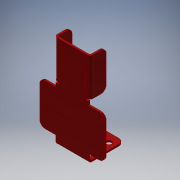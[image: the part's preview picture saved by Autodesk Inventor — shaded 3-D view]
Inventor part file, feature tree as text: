
AUTODESK INVENTOR PART (.ipt)
format: ipt  version: 2018 (Build 220112000, 112)  size: 207,872 bytes
history: native  units: mm
features: other x28, sketch x7, reference x4, hole x1
ambient origin geometry x8: Origin, YZ Plane, XZ Plane, XY Plane, X Axis, Y Axis, Z Axis, Center Point
bodies: Solido1 (feature_tree)
feature tree (40):
  other  "Supporto pistone pinza"
  other  "Faccia1"
  other  "Flangia1"
  hole  "Foro1"  [1 undecoded]
  other  "Flangia3"
  other  "Flangia4"
  other  "Flangia5"
  other  "Flangia6"
  other  "Arrotondamento angolo1"
  sketch  "Schizzo1"
  other  "Piano1"
  sketch  "Schizzo2"
  other  "Piano2"
  other  "Piega (Bend)1"
  other  "Angolo1"
  sketch  "Schizzo4"
  reference  "Riferimento1"
  reference  "Riferimento2"
  reference  "Riferimento3"
  reference  "Riferimento4"
  sketch  "Schizzo5"
  other  "Piano4"
  other  "Piega (Bend)3"
  other  "Angolo3"
  sketch  "Schizzo6"
  other  "Piano5"
  other  "Piega (Bend)4"
  other  "Angolo4"
  sketch  "Schizzo7"
  other  "Piano6"
  other  "Piega (Bend)5"
  other  "Angolo5"
  sketch  "Schizzo8"
  other  "Piano7"
  other  "Piega (Bend)6"
  other  "Angolo6"
  other  "<userpath>\no-brim\Meccanica\Prova Inventor\Assieme 1 - Trasporto.iam"
  other  "Assieme 1 - Trasporto.iam"
  other  "536331 ADN-16-50-A-P-A---(asm_0):1"
  other  "536218 ADN-50-P---(Z):1"
note: 1 required parameter value undecoded (feature->parameter linkage not recoverable at this tier; creation-order binding heuristic only, values carry confidence <= 0.55)
